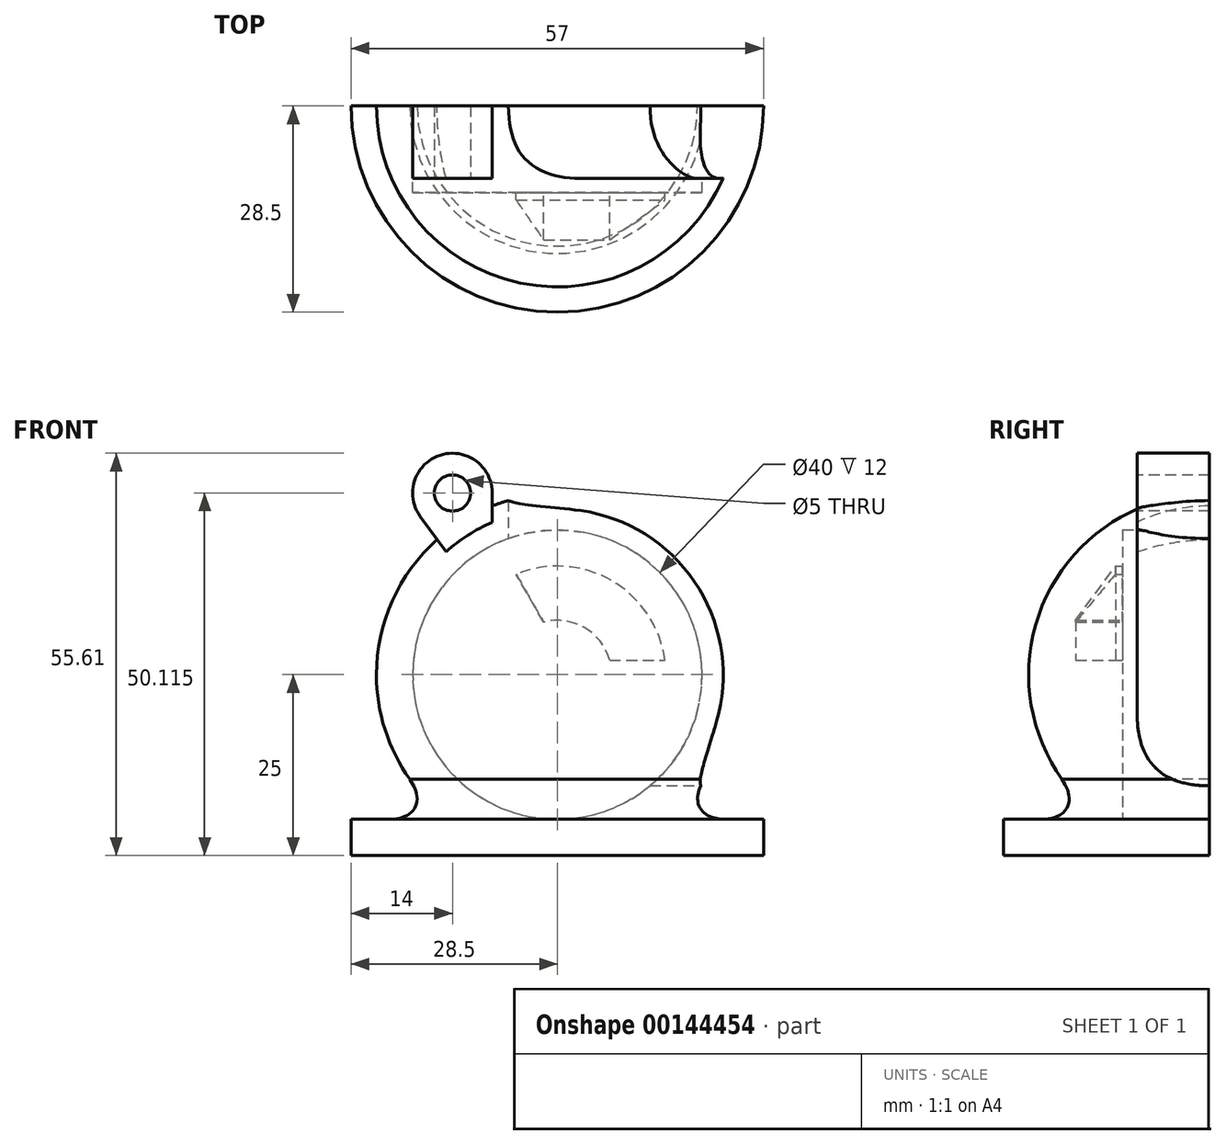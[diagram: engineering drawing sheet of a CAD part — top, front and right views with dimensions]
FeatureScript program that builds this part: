
annotation { "Feature Type Name" : "Feature", "Feature Type Description" : "" }
export const myFeature = defineFeature(function(context is Context, id is Id, definition is map)
    precondition{}
    {
        {
            var Q0;
            Q0=qCreatedBy(makeId("Top.planeOp"),FACE);
            var sketch = newSketch(context, id + "F0", { "sketchPlane" : qUnion([Q0])});
            skLineSegment(sketch, "E0", {"start": v(0, 0) * mm, "end": v(28.5, 0) * mm});
            skLineSegment(sketch, "E1", {"start": v(28.5, 0) * mm, "end": v(-28.5, 0) * mm});
            skArc(sketch, "E2", {"start": v(-28.5, 0) * mm, "mid": v(0, -28.5) * mm, "end": v(28.5, 0) * mm});
            skSolve(sketch);
        }
        {
            var Q0;
            Q0=qCreatedBy(makeId("Front.planeOp"),FACE);
            var sketch = newSketch(context, id + "F1", { "sketchPlane" : qUnion([Q0])});
            skArc(sketch, "E3", {"start": v(-25, 25) * mm, "mid": v(0, 0) * mm, "end": v(25, 25) * mm});
            skLineSegment(sketch, "E4", {"start": v(25, 25) * mm, "end": v(-25, 25) * mm});
            skSolve(sketch);
        }
        {
            var Q0;
            Q0=makeQuery(id+"F1.imprint","IMPRINT",FACE,{"disambiguationData":[TD([[makeQuery(id+"F1.imprint","IMPRINT",EDGE,{"derivedFrom":sQuery(id+"F1.wireOp",EDGE,"E3")}),1.0]])]});
            var Q1;
            Q1=sQuery(id+"F1.wireOp",EDGE,"E4");
            revolve(context, id + "F2", {"entities" : qUnion([Q0]), "axis" : qUnion([Q1]), "revolveType" : RevolveType.ONE_DIRECTION, "angle" : 180 * degree});
        }
        {
            var Q0;
            {var subQ0=sQuery(id+"F0.wireOp",EDGE,"E2");Q0=makeQuery(id+"F0.imprint","IMPRINT",FACE,{"disambiguationData":[TD([[makeQuery(id+"F0.imprint","IMPRINT",EDGE,{"derivedFrom":subQ0}),1.0]])]});}
            extrude(context, id + "F3", {"entities" : qUnion([Q0]), "operationType" : NewBodyOperationType.ADD, "depth" : 5 * mm});
        }
        {
            var Q0;
            Q0=makeQuery(id+"F3.boolean.opBoolean","MERGE",FACE,{"derivedFrom":[makeQuery(id+"F2.opRevolve","CAP_FACE",FACE,{"disambiguationData":[OSD([sQuery(id+"F1.wireOp",EDGE,"E3"),sQuery(id+"F1.wireOp",EDGE,"E4")])],"isStart":true}),makeQuery(id+"F3.opExtrude","SWEPT_FACE",FACE,{"disambiguationData":[OSD([sQuery(id+"F0.wireOp",EDGE,"E1")])]})]});
            var sketch = newSketch(context, id + "F4", { "sketchPlane" : qUnion([Q0])});
            skCircle(sketch, "E5", {"center": v(0, 25) * mm, "radius": 20 * mm});
            skSolve(sketch);
        }
        {
            var Q0;
            Q0=makeQuery(id+"F4.imprint","IMPRINT",FACE,{"disambiguationData":[TD([[makeQuery(id+"F4.imprint","IMPRINT",EDGE,{"derivedFrom":sQuery(id+"F4.wireOp",EDGE,"E5")}),1.0]])]});
            extrude(context, id + "F5", {"entities" : qUnion([Q0]), "operationType" : NewBodyOperationType.REMOVE, "oppositeDirection" : true, "depth" : 12 * mm});
        }
        {
            var Q0;
            Q0=makeQuery(id+"F5.boolean.opBoolean","COPY",FACE,{"derivedFrom":makeQuery(id+"F5.opExtrude","CAP_FACE",FACE,{"disambiguationData":[OSD([sQuery(id+"F4.wireOp",EDGE,"E5")])],"isStart":false})});
            var sketch = newSketch(context, id + "F6", { "sketchPlane" : qUnion([Q0])});
            skArc(sketch, "E6", {"start": v(5.35, 30.26) * mm, "mid": v(-1.88, 32.26) * mm, "end": v(-7.23, 27) * mm});
            skArc(sketch, "E7", {"start": v(9.17, 36.87) * mm, "mid": v(-7.5, 38) * mm, "end": v(-14.87, 23) * mm});
            skLineSegment(sketch, "E8", {"start": v(-7.23, 23) * mm, "end": v(-14.87, 23) * mm, "construction": true});
            skLineSegment(sketch, "E9", {"start": v(0, 25) * mm, "end": v(-15, 25) * mm, "construction": true});
            skLineSegment(sketch, "E10", {"start": v(-7.23, 27) * mm, "end": v(-14.87, 27) * mm});
            skLineSegment(sketch, "E11", {"start": v(-11.05, 27) * mm, "end": v(-11.05, 25) * mm, "construction": true});
            skLineSegment(sketch, "E12", {"start": v(-11.05, 23) * mm, "end": v(-11.05, 25) * mm, "construction": true});
            skLineSegment(sketch, "E13", {"start": v(1.88, 32.26) * mm, "end": v(5.7, 38.87) * mm});
            skLineSegment(sketch, "E14", {"start": v(5.35, 30.26) * mm, "end": v(9.17, 36.87) * mm, "construction": true});
            skLineSegment(sketch, "E15", {"start": v(0, 25) * mm, "end": v(14.84, 50.7) * mm, "construction": true});
            skLineSegment(sketch, "E16", {"start": v(5.5, 34.52) * mm, "end": v(7.23, 33.52) * mm});
            skLineSegment(sketch, "E17", {"start": v(5.5, 34.52) * mm, "end": v(3.77, 35.52) * mm});
            skSolve(sketch);
        }
        {
            var Q0;
            Q0=makeQuery(id+"F3.boolean.opBoolean","MERGE",FACE,{"derivedFrom":[makeQuery(id+"F2.opRevolve","CAP_FACE",FACE,{"disambiguationData":[OSD([sQuery(id+"F1.wireOp",EDGE,"E3"),sQuery(id+"F1.wireOp",EDGE,"E4")])],"isStart":true}),makeQuery(id+"F3.opExtrude","SWEPT_FACE",FACE,{"disambiguationData":[OSD([sQuery(id+"F0.wireOp",EDGE,"E1")])]})]});
            cPlane(context, id + "F7", {"entities" : qUnion([Q0]), "cplaneType" : CPlaneType.OFFSET, "offset" : 10 * mm, "oppositeDirection" : true, "width" : 150 * mm, "height" : 150 * mm});
        }
        {
            var Q0;
            {var subQ6=sQuery(id+"F6.wireOp",EDGE,"E10");Q0=makeQuery(id+"F6.imprint","IMPRINT",FACE,{"disambiguationData":[TD([[makeQuery(id+"F6.imprint","IMPRINT",EDGE,{"derivedFrom":subQ6}),-1.0]])]});}
            var Q1;
            Q1=makeQuery(id+"F2.opRevolve","SWEPT_FACE",FACE,{"disambiguationData":[OSD([sQuery(id+"F1.wireOp",EDGE,"E3")])]});
            extrude(context, id + "F8", {"entities" : qUnion([Q0]), "operationType" : NewBodyOperationType.REMOVE, "oppositeDirection" : true, "endBoundEntityFace" : qUnion([Q1]), "depth" : 6.5 * mm});
        }
        {
            var Q0;
            Q0=qCreatedBy(makeId("Right.planeOp"),FACE);
            var sketch = newSketch(context, id + "F9", { "sketchPlane" : qUnion([Q0])});
            skLineSegment(sketch, "E18.0", {"start": v(0, 45) * mm, "end": v(0, 5) * mm});
            skLineSegment(sketch, "E19", {"start": v(0, 25) * mm, "end": v(-42.33, 25) * mm});
            skSolve(sketch);
        }
        {
            var Q0;
            Q0=makeQuery(id+"F8.boolean.opBoolean","COPY",EDGE,{"derivedFrom":makeQuery(id+"F8.opExtrude","CAP_EDGE",EDGE,{"disambiguationData":[OSD([sQuery(id+"F6.wireOp",EDGE,"E7")])],"isStart":false})});
            var Q1;
            Q1=makeQuery(id+"FMHrgSVFdLp09on_1.2.F8.boolean.opBoolean","COPY",EDGE,{"derivedFrom":makeQuery(id+"FMHrgSVFdLp09on_1.2.F8.opExtrude","CAP_EDGE",EDGE,{"disambiguationData":[OSD([sQuery(id+"F6.wireOp",EDGE,"E7")])],"isStart":false})});
            var Q2;
            Q2=makeQuery(id+"FMHrgSVFdLp09on_1.1.F8.boolean.opBoolean","COPY",EDGE,{"derivedFrom":makeQuery(id+"FMHrgSVFdLp09on_1.1.F8.opExtrude","CAP_EDGE",EDGE,{"disambiguationData":[OSD([sQuery(id+"F6.wireOp",EDGE,"E7")])],"isStart":false})});
            chamfer(context, id + "F10", {"entities" : qUnion([Q0, Q1, Q2]), "chamferType" : ChamferType.TWO_OFFSETS, "width1" : 7.5 * mm, "oppositeDirection" : false, "width2" : 5.5 * mm, "tangentPropagation" : true});
        }
        {
            var Q0;
            Q0=makeQuery(id+"F3.boolean.opBoolean","MERGE",FACE,{"derivedFrom":[makeQuery(id+"F2.opRevolve","CAP_FACE",FACE,{"disambiguationData":[OSD([sQuery(id+"F1.wireOp",EDGE,"E3"),sQuery(id+"F1.wireOp",EDGE,"E4")])],"isStart":true}),makeQuery(id+"F3.opExtrude","SWEPT_FACE",FACE,{"disambiguationData":[OSD([sQuery(id+"F0.wireOp",EDGE,"E1")])]})]});
            var sketch = newSketch(context, id + "F11", { "sketchPlane" : qUnion([Q0])});
            skLineSegment(sketch, "E20", {"start": v(0, 25) * mm, "end": v(14.5, 50.11) * mm, "construction": true});
            skLineSegment(sketch, "E21", {"start": v(0, 25) * mm, "end": v(-25, 25) * mm, "construction": true});
            skArc(sketch, "E22", {"start": v(18.95, 46.88) * mm, "mid": v(13.36, 55.5) * mm, "end": v(11.75, 45.35) * mm});
            skLineSegment(sketch, "E23", {"start": v(18.95, 46.88) * mm, "end": v(16.62, 43.68) * mm});
            skLineSegment(sketch, "E24", {"start": v(14.5, 50.11) * mm, "end": v(9.74, 52.86) * mm});
            skSolve(sketch);
        }
        {
            var Q0;
            Q0=qCreatedBy(id+"F7.planeOp",FACE);
            var sketch = newSketch(context, id + "F12", { "sketchPlane" : qUnion([Q0])});
            skPoint(sketch, "E25.0", {"position": v(16.62, 43.68) * mm});
            skArc(sketch, "E26.0", {"start": v(18.95, 46.88) * mm, "mid": v(16.2, 55.35) * mm, "end": v(9, 50.11) * mm});
            skLineSegment(sketch, "E27.0.1", {"start": v(-15, 5) * mm, "end": v(15, 5) * mm});
            skLineSegment(sketch, "E28.0", {"start": v(18.95, 46.88) * mm, "end": v(16.62, 43.68) * mm});
            skArc(sketch, "E29", {"start": v(9, 46.07) * mm, "mid": v(12.36, 44.3) * mm, "end": v(15.39, 41.98) * mm});
            skLineSegment(sketch, "E30", {"start": v(18.95, 46.88) * mm, "end": v(15.39, 41.98) * mm});
            skLineSegment(sketch, "E31", {"start": v(9, 50.11) * mm, "end": v(9, 46.07) * mm});
            skPoint(sketch, "E32.orphan", {"position": v(11.75, 45.35) * mm});
            skPoint(sketch, "E33.orphan", {"position": v(-11.18, 5) * mm});
            skPoint(sketch, "E34.orphan", {"position": v(11.18, 5) * mm});
            skLineSegment(sketch, "E35", {"start": v(9, 50.11) * mm, "end": v(14.5, 50.11) * mm});
            skSolve(sketch);
        }
        {
            var Q0;
            {var subQ0=sQuery(id+"F12.wireOp",EDGE,"E26.0");Q0=makeQuery(id+"F12.imprint","IMPRINT",FACE,{"disambiguationData":[TD([[makeQuery(id+"F12.imprint","IMPRINT",EDGE,{"derivedFrom":subQ0}),1.0]])]});}
            var Q1;
            Q1=makeQuery(id+"F3.boolean.opBoolean","MERGE",FACE,{"derivedFrom":[makeQuery(id+"F2.opRevolve","CAP_FACE",FACE,{"disambiguationData":[OSD([sQuery(id+"F1.wireOp",EDGE,"E3"),sQuery(id+"F1.wireOp",EDGE,"E4")])],"isStart":true}),makeQuery(id+"F3.opExtrude","SWEPT_FACE",FACE,{"disambiguationData":[OSD([sQuery(id+"F0.wireOp",EDGE,"E1")])]})]});
            extrude(context, id + "F13", {"entities" : qUnion([Q0]), "operationType" : NewBodyOperationType.ADD, "endBound" : BoundingType.UP_TO_SURFACE, "endBoundEntityFace" : qUnion([Q1]), "depth" : 25 * mm});
        }
        {
            var Q0;
            {var subQ0=sQuery(id+"F1.wireOp",EDGE,"E4");var subQ1=sQuery(id+"F1.wireOp",EDGE,"E3");var subQ2=sQuery(id+"F0.wireOp",EDGE,"E1");Q0=makeQuery(id+"F13.boolean.opBoolean","MERGE",FACE,{"derivedFrom":[makeQuery(id+"F3.boolean.opBoolean","MERGE",FACE,{"derivedFrom":[makeQuery(id+"F2.opRevolve","CAP_FACE",FACE,{"disambiguationData":[OSD([subQ1,subQ0])],"isStart":true}),makeQuery(id+"F3.opExtrude","SWEPT_FACE",FACE,{"disambiguationData":[OSD([subQ2])]})]}),makeQuery(id+"F13.opExtrude","CAP_FACE",FACE,{"disambiguationData":[OSD([subQ2,subQ1,subQ0])],"isStart":false})]});}
            var sketch = newSketch(context, id + "F14", { "sketchPlane" : qUnion([Q0])});
            skPoint(sketch, "E36", {"position": v(14.5, 50.11) * mm});
            skSolve(sketch);
        }
        {
            var Q0;
            Q0=sQuery(id+"F14.wireOp",VERTEX,"E36");
            var Q1;
            Q1=makeQuery(id+"F2.opRevolve","SWEPT_BODY",BODY,{"disambiguationData":[OSD([sQuery(id+"F1.wireOp",EDGE,"E3"),sQuery(id+"F1.wireOp",EDGE,"E4")])]});
            hole(context, id + "F15", {"style" : HoleStyle.SIMPLE, "endStyle" : HoleEndStyle.THROUGH, "holeDiameter" : 5 * mm, "startFromSketch" : true, "locations" : qUnion([Q0]), "scope" : qUnion([Q1]), "isTappedThrough" : true});
        }
        {
            var Q0;
            {var subQ0=sQuery(id+"F1.wireOp",EDGE,"E4");var subQ1=sQuery(id+"F1.wireOp",EDGE,"E3");var subQ2=sQuery(id+"F0.wireOp",EDGE,"E1");Q0=makeQuery(id+"F13.boolean.opBoolean","MERGE",FACE,{"derivedFrom":[makeQuery(id+"F3.boolean.opBoolean","MERGE",FACE,{"derivedFrom":[makeQuery(id+"F2.opRevolve","CAP_FACE",FACE,{"disambiguationData":[OSD([subQ1,subQ0])],"isStart":true}),makeQuery(id+"F3.opExtrude","SWEPT_FACE",FACE,{"disambiguationData":[OSD([subQ2])]})]}),makeQuery(id+"F13.opExtrude","CAP_FACE",FACE,{"disambiguationData":[OSD([subQ2,subQ1,subQ0])],"isStart":false})]});}
            var sketch = newSketch(context, id + "F16", { "sketchPlane" : qUnion([Q0])});
            skLineSegment(sketch, "E37", {"start": v(6.76, 49.07) * mm, "end": v(6.76, 43.82) * mm});
            skLineSegment(sketch, "E38", {"start": v(-19.72, 9.64) * mm, "end": v(-12.8, 9.64) * mm});
            skArc(sketch, "E39.0", {"start": v(6.76, 43.82) * mm, "mid": v(-17.36, 34.94) * mm, "end": v(-12.8, 9.64) * mm});
            skArc(sketch, "E40.0", {"start": v(9, 48.32) * mm, "mid": v(-20.07, 39.9) * mm, "end": v(-19.72, 9.64) * mm});
            skPoint(sketch, "E41.orphan", {"position": v(-15, 5) * mm});
            skSolve(sketch);
        }
        {
            var Q0;
            {var subQ0=sQuery(id+"F16.wireOp",EDGE,"E37");Q0=makeQuery(id+"F16.imprint","IMPRINT",FACE,{"disambiguationData":[TD([[makeQuery(id+"F16.imprint","IMPRINT",EDGE,{"derivedFrom":subQ0}),-1.0]])]});}
            extrude(context, id + "F17", {"entities" : qUnion([Q0]), "operationType" : NewBodyOperationType.REMOVE, "oppositeDirection" : true, "depth" : 10 * mm});
        }
        {
            var Q0;
            Q0=makeQuery(id+"F17.boolean.opBoolean","COPY",EDGE,{"derivedFrom":makeQuery(id+"F17.opExtrude","CAP_EDGE",EDGE,{"disambiguationData":[OSD([sQuery(id+"F16.wireOp",EDGE,"E37")])],"isStart":false})});
            var Q1;
            Q1=makeQuery(id+"F17.boolean.opBoolean","COPY",EDGE,{"derivedFrom":makeQuery(id+"F17.opExtrude","CAP_EDGE",EDGE,{"disambiguationData":[OSD([sQuery(id+"F16.wireOp",EDGE,"E38")])],"isStart":false})});
            fillet(context, id + "F18", {"entities" : qUnion([Q0, Q1]), "radius" : 10 * mm, "tangentPropagation" : true, "rho" : 0.5, "crossSection" : FilletCrossSection.CONIC, "allowEdgeOverflow" : false});
        }
        {
            var Q0;
            Q0=makeQuery(id+"F3.boolean.opBoolean","INTERSECT",EDGE,{"derivedFrom":[makeQuery(id+"F2.opRevolve","SWEPT_FACE",FACE,{"disambiguationData":[OSD([sQuery(id+"F1.wireOp",EDGE,"E3")])]}),makeQuery(id+"F3.opExtrude","CAP_FACE",FACE,{"disambiguationData":[OSD([sQuery(id+"F0.wireOp",EDGE,"E1"),sQuery(id+"F0.wireOp",EDGE,"E2")])],"isStart":false})]});
            fillet(context, id + "F19", {"entities" : qUnion([Q0]), "radius" : 3.5 * mm, "tangentPropagation" : true, "rho" : .4, "crossSection" : FilletCrossSection.CONIC, "allowEdgeOverflow" : false});
        }
    });
